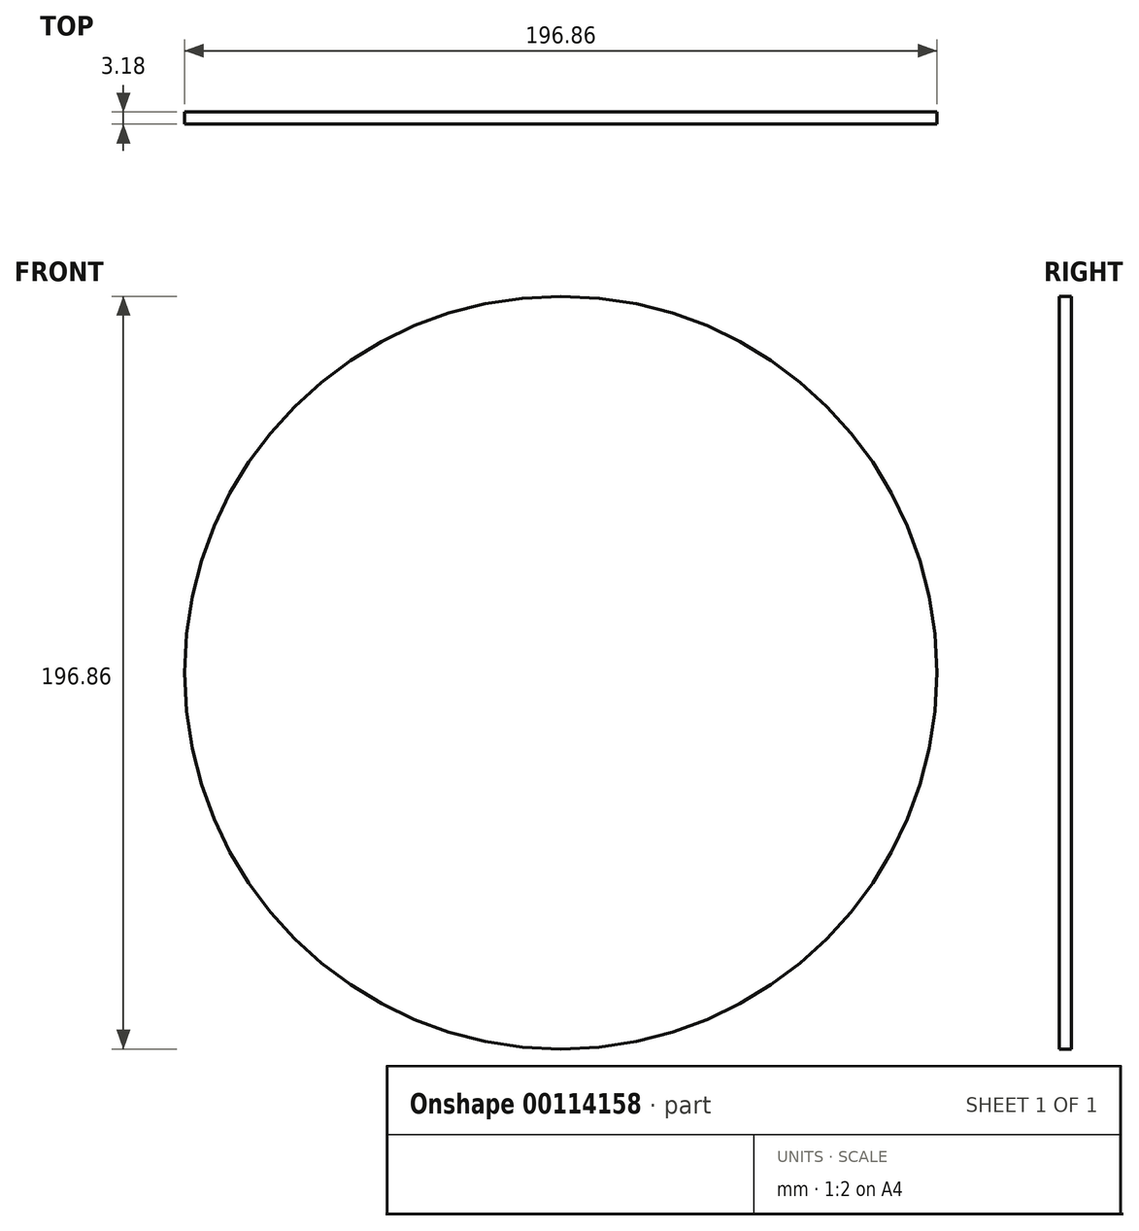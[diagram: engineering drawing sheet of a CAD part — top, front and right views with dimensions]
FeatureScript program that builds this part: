
annotation { "Feature Type Name" : "Feature", "Feature Type Description" : "" }
export const myFeature = defineFeature(function(context is Context, id is Id, definition is map)
    precondition{}
    {
        {
            var Q0;
            Q0=qCreatedBy(makeId("Front.planeOp"),FACE);
            var sketch = newSketch(context, id + "F0", { "sketchPlane" : qUnion([Q0])});
            skCircle(sketch, "E0", {"center": v(0, 0) * mm, "radius": 98.42 * mm});
            skSolve(sketch);
        }
        {
            var Q0;
            Q0=makeQuery(id+"F0.imprint","IMPRINT",FACE,{"disambiguationData":[TD([[makeQuery(id+"F0.imprint","IMPRINT",EDGE,{"derivedFrom":sQuery(id+"F0.wireOp",EDGE,"E0")}),1.0]])]});
            extrude(context, id + "F1", {"entities" : qUnion([Q0]), "oppositeDirection" : true, "depth" : 3.17 * mm});
        }
    });
